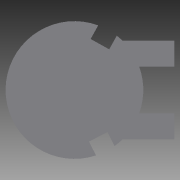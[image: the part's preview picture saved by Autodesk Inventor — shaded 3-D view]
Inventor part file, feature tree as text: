
AUTODESK INVENTOR PART (.ipt)
format: ipt  version: 2014 (Build 180170000, 170)  size: 197,120 bytes
history: native  units: mm
features: extrude x11, other x7, sketch x4
ambient origin geometry x8: Origin, YZ Plane, XZ Plane, XY Plane, X Axis, Y Axis, Z Axis, Center Point
bodies: Body1 (feature_tree)
feature tree (22):
  other  "Teller"
  other  "Dicke Stifte Außen"
  other  "Dünne Stifte Außen"
  other  "Dicke Stifte Vorn"
  other  "Dicke Stifte Hinten"
  other  "Dünne Stifte Vorn"
  other  "Dünne Stifte Hinten"
  extrude  "Extrusion13"  Depth=6.0mm
  extrude  "Extrusion14"  Depth=53.0mm
  extrude  "Extrusion15"  Depth=2.0mm
  extrude  "Extrusion16"  Depth=2.0mm TaperAngle=360.0deg
  extrude  "Extrusion17"  Depth=2.0mm
  extrude  "Extrusion18"  Depth=2.0mm
  extrude  "Extrusion19"  Depth=2.0mm
  extrude  "Extrusion21"  Depth=2.0mm
  extrude  "Extrusion22"  Depth=8.0mm TaperAngle=0.0deg
  extrude  "Extrusion23"  Depth=4.0mm TaperAngle=0.0deg
  extrude  "Extrusion24"  Depth=4.0mm TaperAngle=0.0deg
  sketch  "Skizze18"  dims[d24=53.0mm d55=6.0mm]
  sketch  "Skizze19"  dims[d83=3.5mm d84=53.0mm]
  sketch  "Skizze20"  dims[d85=80.0mm d87=360.0deg d90=2.0mm]
  sketch  "Skizze21"  dims[d91=53.0mm d92=53.0mm d93=80.0mm d95=360.0deg d97=3.5mm d99=3.5mm d100=2.0mm d101=2.0mm d104=8.0mm d105=0.0mm d106=4.0mm d107=0.0mm d108=4.0mm d109=0.0mm d110=10.0mm d111=0.0mm d112=10.0mm d113=0.0mm d114=6.0mm d115=0.0mm d118=6.0mm d119=6.0mm d123=18.0mm d125=2.0mm d126=0.0mm d131=2.0mm d132=0.0mm d133=2.0mm d134=0.0mm d135=3.0mm d136=2.0mm d137=0.0mm d138=3.0mm d139=2.0mm d140=0.0mm]
